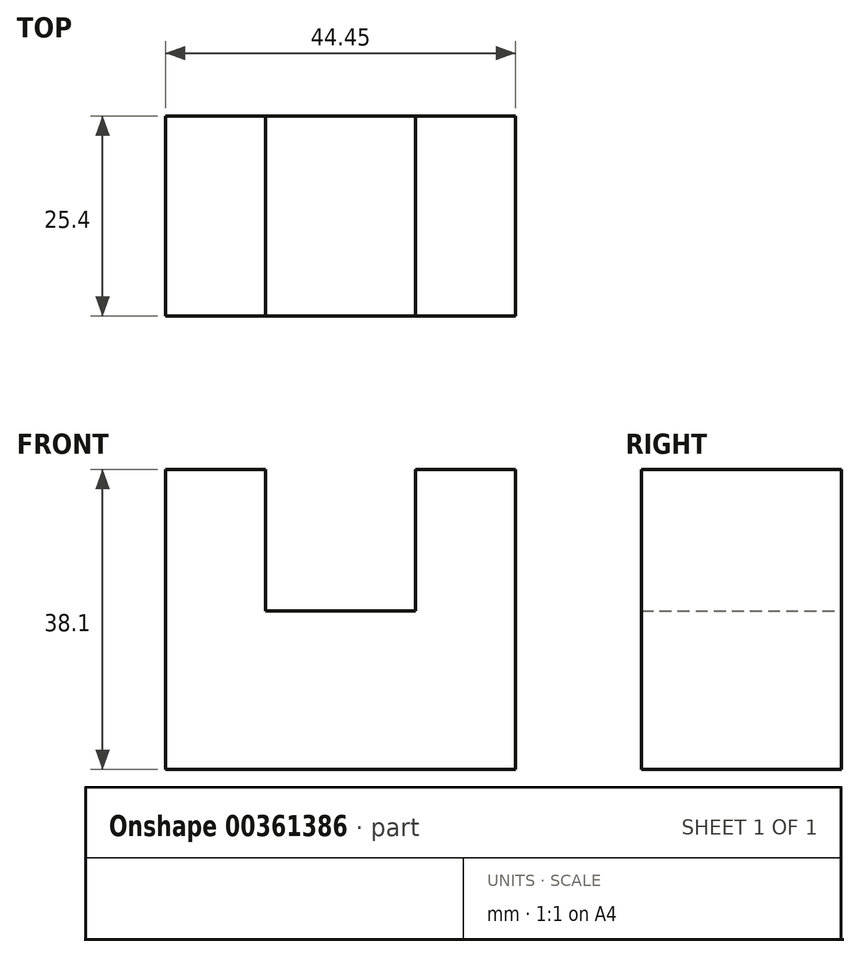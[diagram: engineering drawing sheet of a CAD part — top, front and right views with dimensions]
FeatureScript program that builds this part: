
annotation { "Feature Type Name" : "Feature", "Feature Type Description" : "" }
export const myFeature = defineFeature(function(context is Context, id is Id, definition is map)
    precondition{}
    {
        {
            var Q0;
            Q0=qCreatedBy(makeId("Front.planeOp"),FACE);
            var sketch = newSketch(context, id + "F0", { "sketchPlane" : qUnion([Q0])});
            skLineSegment(sketch, "E0", {"start": v(-52.68, 27.4) * mm, "end": v(-39.98, 27.4) * mm});
            skLineSegment(sketch, "E1", {"start": v(-39.98, 27.4) * mm, "end": v(-39.98, 9.45) * mm});
            skLineSegment(sketch, "E2", {"start": v(-39.98, 9.45) * mm, "end": v(-20.93, 9.45) * mm});
            skLineSegment(sketch, "E3", {"start": v(-20.93, 9.45) * mm, "end": v(-20.93, 27.4) * mm});
            skLineSegment(sketch, "E4", {"start": v(-20.93, 27.4) * mm, "end": v(-8.23, 27.4) * mm});
            skLineSegment(sketch, "E5", {"start": v(-8.23, 27.4) * mm, "end": v(-8.23, -10.7) * mm});
            skLineSegment(sketch, "E6", {"start": v(-8.23, -10.7) * mm, "end": v(-52.68, -10.7) * mm});
            skLineSegment(sketch, "E7", {"start": v(-52.68, -10.7) * mm, "end": v(-52.68, 27.4) * mm});
            skSolve(sketch);
        }
        {
            var Q0;
            Q0 = qSketchRegion(id + "F0", true);
            extrude(context, id + "F1", {"entities" : qUnion([Q0]), "depth" : 25.4 * mm});
        }
    });
